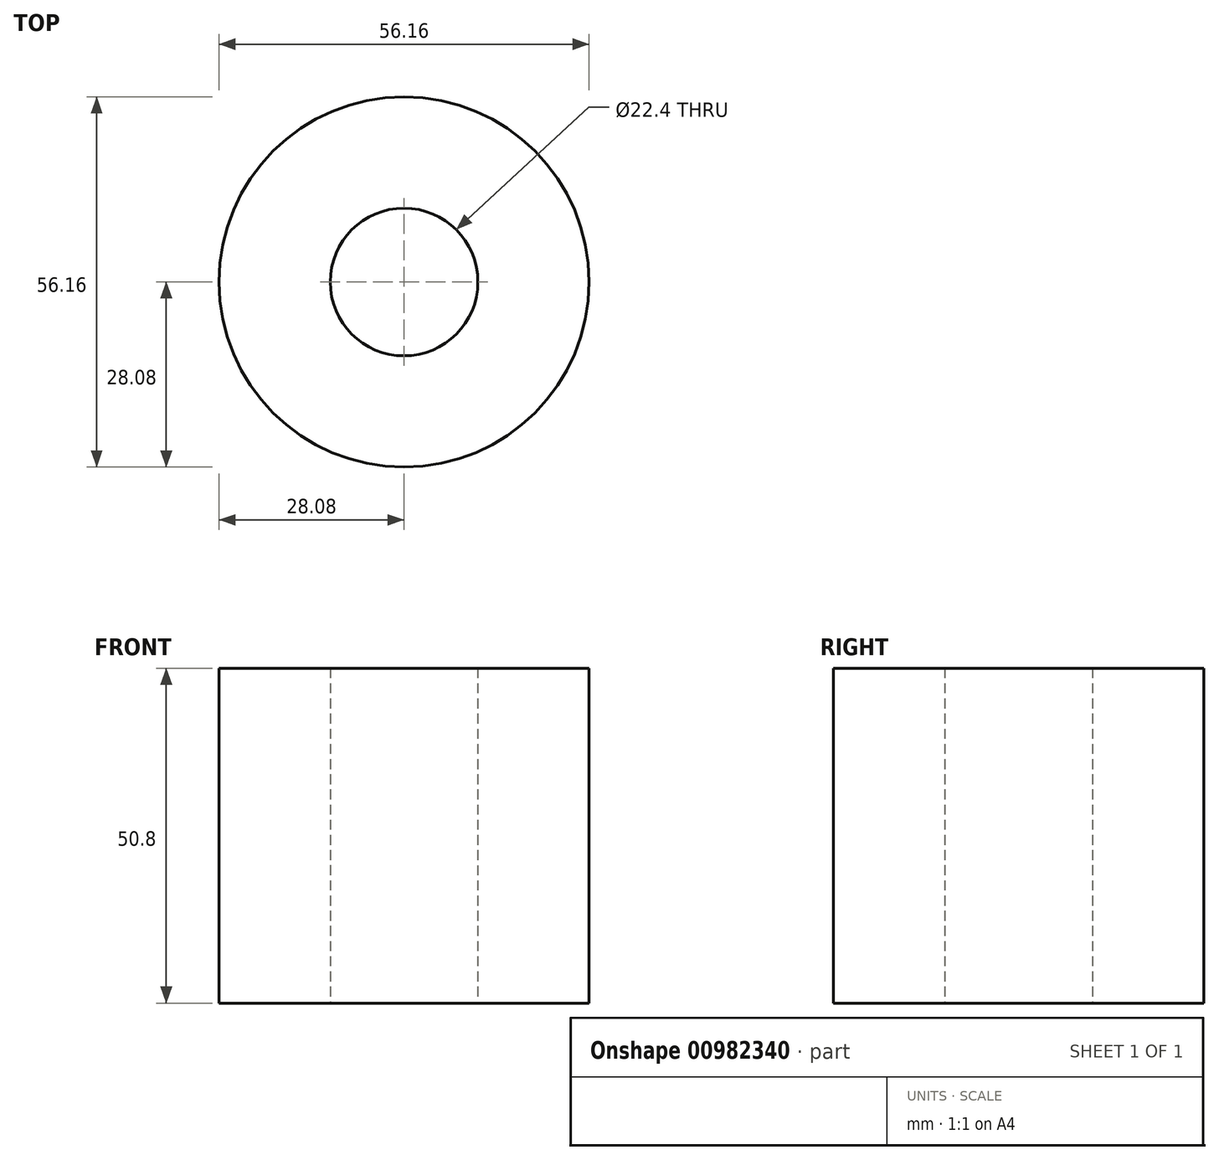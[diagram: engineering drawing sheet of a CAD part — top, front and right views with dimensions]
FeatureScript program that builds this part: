
annotation { "Feature Type Name" : "Feature", "Feature Type Description" : "" }
export const myFeature = defineFeature(function(context is Context, id is Id, definition is map)
    precondition{}
    {
        {
            var Q0;
            Q0=qCreatedBy(makeId("Top.planeOp"),FACE);
            var sketch = newSketch(context, id + "F0", { "sketchPlane" : qUnion([Q0])});
            skCircle(sketch, "E0", {"center": v(0, 0) * mm, "radius": 28.08 * mm});
            skCircle(sketch, "E1", {"center": v(0, 0) * mm, "radius": 11.2 * mm});
            skSolve(sketch);
        }
        {
            var Q0;
            Q0=makeQuery(id+"F0.imprint","IMPRINT",FACE,{"disambiguationData":[TD([[makeQuery(id+"F0.imprint","IMPRINT",EDGE,{"derivedFrom":sQuery(id+"F0.wireOp",EDGE,"E0")}),1.0]])]});
            extrude(context, id + "F1", {"entities" : qUnion([Q0]), "depth" : 50.8 * mm, "offsetDistance" : 25.4 * mm});
        }
    });
